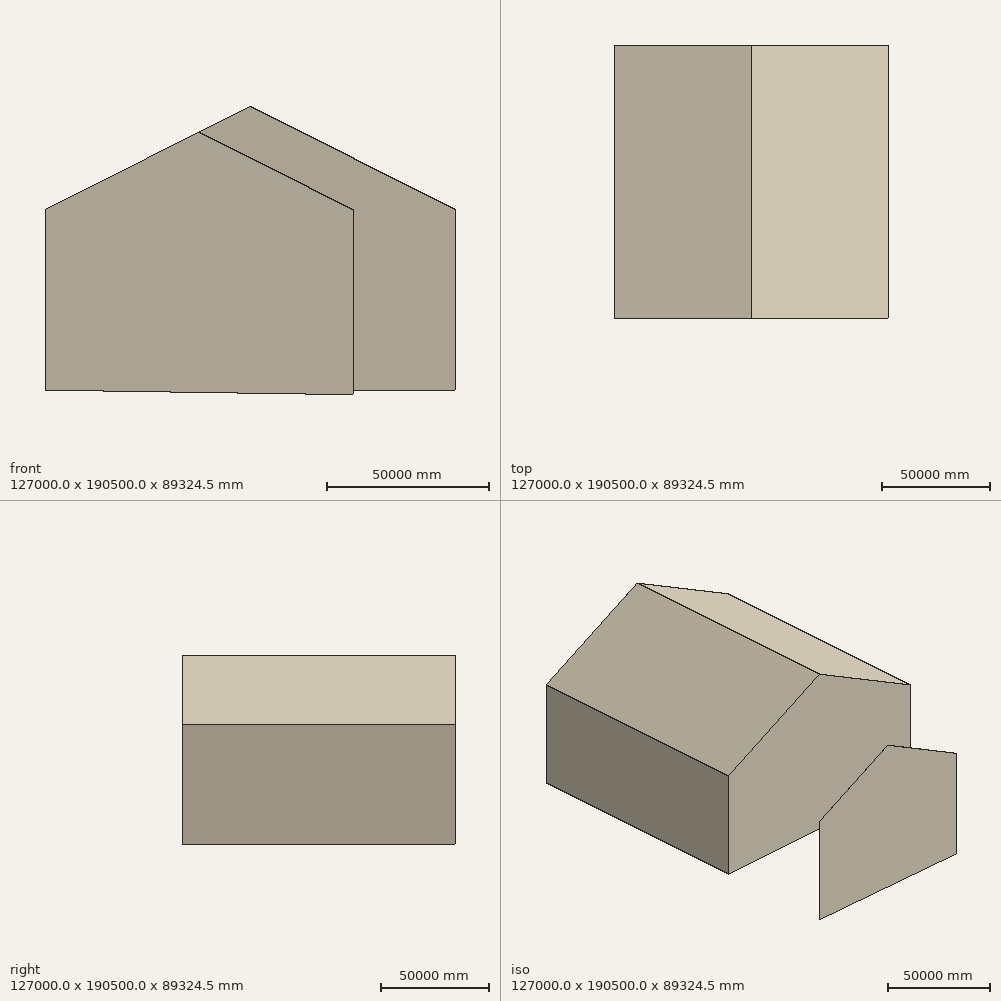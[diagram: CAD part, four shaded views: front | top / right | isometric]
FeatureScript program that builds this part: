
annotation { "Feature Type Name" : "Feature", "Feature Type Description" : "" }
export const myFeature = defineFeature(function(context is Context, id is Id, definition is map)
    precondition{}
    {
        {
            var Q0;
            Q0=qCreatedBy(makeId("Front.planeOp"),FACE);
            var sketch = newSketch(context, id + "F0", { "sketchPlane" : qUnion([Q0])});
            skLineSegment(sketch, "E0.bottom", {"start": v(63500, -27940) * mm, "end": v(-63500, -27940) * mm});
            skLineSegment(sketch, "E0.top", {"start": v(63500, 27940) * mm, "end": v(-63500, 27940) * mm});
            skLineSegment(sketch, "E0.left", {"start": v(63500, -27940) * mm, "end": v(63500, 27940) * mm});
            skLineSegment(sketch, "E0.right", {"start": v(-63500, -27940) * mm, "end": v(-63500, 27940) * mm});
            skPoint(sketch, "E0.middle", {"position": v(0, 0) * mm});
            skSolve(sketch);
        }
        {
            var Q0;
            Q0=makeQuery(id+"F0.imprint","IMPRINT",FACE,{"disambiguationData":[TD([[makeQuery(id+"F0.imprint","IMPRINT",EDGE,{"derivedFrom":sQuery(id+"F0.wireOp",EDGE,"E0.bottom")}),-1.0]])]});
            extrude(context, id + "F1", {"entities" : qUnion([Q0]), "depth" : 127000 * mm, "offsetDistance" : 25.4 * mm});
        }
        {
            var Q0;
            Q0=makeQuery(id+"F1.opExtrude","CAP_FACE",FACE,{"disambiguationData":[OSD([sQuery(id+"F0.wireOp",EDGE,"E0.bottom"),sQuery(id+"F0.wireOp",EDGE,"E0.top"),sQuery(id+"F0.wireOp",EDGE,"E0.left"),sQuery(id+"F0.wireOp",EDGE,"E0.right")])],"isStart":false});
            var sketch = newSketch(context, id + "F2", { "sketchPlane" : qUnion([Q0])});
            skLineSegment(sketch, "E1", {"start": v(-63500, 27940) * mm, "end": v(0, 59968.18) * mm});
            skLineSegment(sketch, "E2", {"start": v(0, 59968.18) * mm, "end": v(0, 59968.18) * mm});
            skLineSegment(sketch, "E3", {"start": v(63500, 27940) * mm, "end": v(0, 59968.18) * mm});
            skLineSegment(sketch, "E4", {"start": v(-63500, 27940) * mm, "end": v(63500, 27940) * mm});
            skSolve(sketch);
        }
        {
            var Q0;
            Q0=makeQuery(id+"F2.imprint","IMPRINT",FACE,{"disambiguationData":[TD([[makeQuery(id+"F2.imprint","IMPRINT",EDGE,{"derivedFrom":sQuery(id+"F2.wireOp",EDGE,"E1")}),-1.0]])]});
            extrude(context, id + "F3", {"entities" : qUnion([Q0]), "operationType" : NewBodyOperationType.ADD, "oppositeDirection" : true, "depth" : 127000 * mm, "offsetDistance" : 25.4 * mm});
        }
        {
            var Q0;
            Q0=makeQuery(id+"F3.boolean.opBoolean","MERGE",FACE,{"derivedFrom":[makeQuery(id+"F1.opExtrude","CAP_FACE",FACE,{"disambiguationData":[OSD([sQuery(id+"F0.wireOp",EDGE,"E0.bottom"),sQuery(id+"F0.wireOp",EDGE,"E0.top"),sQuery(id+"F0.wireOp",EDGE,"E0.left"),sQuery(id+"F0.wireOp",EDGE,"E0.right")])],"isStart":false}),makeQuery(id+"F3.opExtrude","CAP_FACE",FACE,{"disambiguationData":[OSD([sQuery(id+"F2.wireOp",EDGE,"E1"),sQuery(id+"F2.wireOp",EDGE,"E3"),sQuery(id+"F2.wireOp",EDGE,"E4")])],"isStart":true})]});
            var sketch = newSketch(context, id + "F4", { "sketchPlane" : qUnion([Q0])});
            skLineSegment(sketch, "E5", {"start": v(-63500, -27940) * mm, "end": v(-63500, 27940) * mm});
            skLineSegment(sketch, "E6", {"start": v(-63500, 27940) * mm, "end": v(-63500, 27940) * mm});
            skLineSegment(sketch, "E7", {"start": v(-15875, 51961.14) * mm, "end": v(-15875, 51961.14) * mm});
            skLineSegment(sketch, "E8", {"start": v(-63500, 27940) * mm, "end": v(-15875, 51961.14) * mm});
            skLineSegment(sketch, "E9", {"start": v(-15875, 51961.14) * mm, "end": v(31750, 27940) * mm});
            skSolve(sketch);
        }
        {
            var Q0;
            Q0=sQuery(id+"F4.wireOp",EDGE,"E9");
            var Q1;
            Q1=sQuery(id+"F4.wireOp",EDGE,"E8");
            var Q2;
            Q2=sQuery(id+"F4.wireOp",EDGE,"E5");
            extrude(context, id + "F5", {"bodyType" : ToolBodyType.SURFACE, "surfaceEntities" : qUnion([Q0, Q1, Q2]), "depth" : 63500 * mm, "offsetDistance" : 25.4 * mm});
        }
        {
            var Q0;
            Q0=makeQuery(id+"F3.boolean.opBoolean","MERGE",FACE,{"derivedFrom":[makeQuery(id+"F1.opExtrude","CAP_FACE",FACE,{"disambiguationData":[OSD([sQuery(id+"F0.wireOp",EDGE,"E0.bottom"),sQuery(id+"F0.wireOp",EDGE,"E0.top"),sQuery(id+"F0.wireOp",EDGE,"E0.left"),sQuery(id+"F0.wireOp",EDGE,"E0.right")])],"isStart":false}),makeQuery(id+"F3.opExtrude","CAP_FACE",FACE,{"disambiguationData":[OSD([sQuery(id+"F2.wireOp",EDGE,"E1"),sQuery(id+"F2.wireOp",EDGE,"E3"),sQuery(id+"F2.wireOp",EDGE,"E4")])],"isStart":true})]});
            cPlane(context, id + "F6", {"entities" : qUnion([Q0]), "cplaneType" : CPlaneType.OFFSET, "offset" : 63500 * mm, "width" : 152.4 * mm, "height" : 152.4 * mm});
        }
        {
            var Q0;
            Q0=qCreatedBy(id+"F6.planeOp",FACE);
            var sketch = newSketch(context, id + "F7", { "sketchPlane" : qUnion([Q0])});
            skLineSegment(sketch, "E10.0", {"start": v(-63500, 27940) * mm, "end": v(-63500, -27940) * mm});
            skLineSegment(sketch, "E11.0", {"start": v(-15875, 51961.14) * mm, "end": v(-63500, 27940) * mm});
            skLineSegment(sketch, "E12.0", {"start": v(31750, 27940) * mm, "end": v(-15875, 51961.14) * mm});
            skLineSegment(sketch, "E13", {"start": v(31750, 27940) * mm, "end": v(31750, -29356.32) * mm});
            skLineSegment(sketch, "E14", {"start": v(31750, -29356.32) * mm, "end": v(-63500, -27940) * mm});
            skSolve(sketch);
        }
        {
            var Q0;
            Q0=makeQuery(id+"F7.imprint","IMPRINT",FACE,{"disambiguationData":[TD([[makeQuery(id+"F7.imprint","IMPRINT",EDGE,{"derivedFrom":sQuery(id+"F7.wireOp",EDGE,"E10.0")}),1.0]])]});
            extrude(context, id + "F8", {"entities" : qUnion([Q0]), "oppositeDirection" : true, "depth" : 25.4 * mm, "offsetDistance" : 25.4 * mm});
        }
    });
